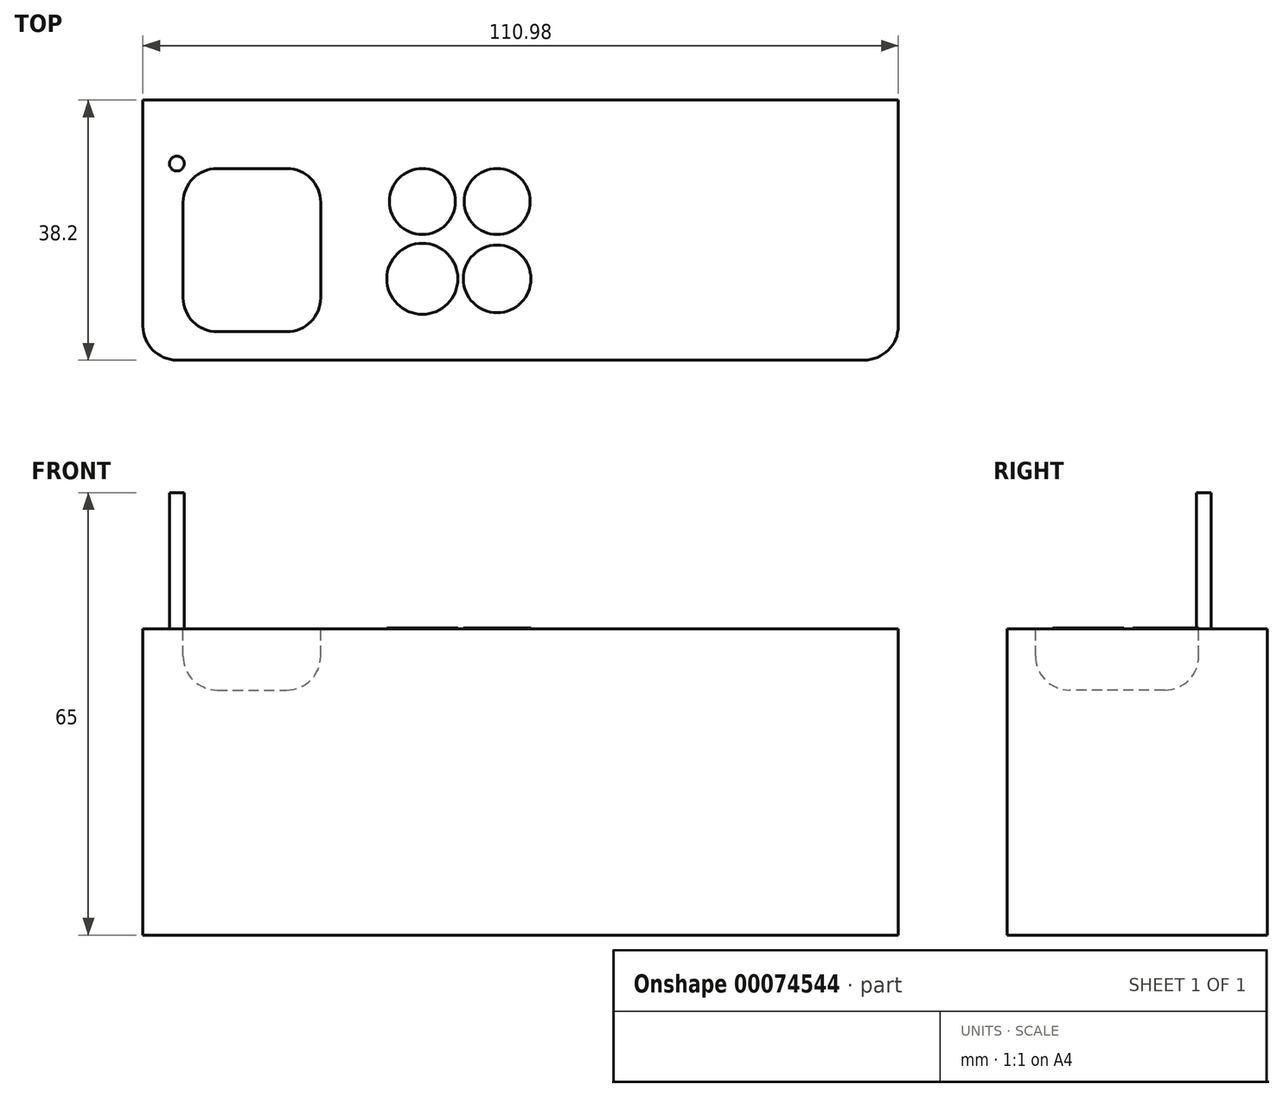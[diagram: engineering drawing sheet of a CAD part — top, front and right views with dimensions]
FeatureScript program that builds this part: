
annotation { "Feature Type Name" : "Feature", "Feature Type Description" : "" }
export const myFeature = defineFeature(function(context is Context, id is Id, definition is map)
    precondition{}
    {
        {
            var Q0;
            Q0=qCreatedBy(makeId("Top.planeOp"),FACE);
            var sketch = newSketch(context, id + "F0", { "sketchPlane" : qUnion([Q0])});
            skLineSegment(sketch, "E0.bottom", {"start": v(-50.94, 18.45) * mm, "end": v(60.04, 18.45) * mm});
            skLineSegment(sketch, "E0.top", {"start": v(-45.94, -19.75) * mm, "end": v(55.04, -19.75) * mm});
            skLineSegment(sketch, "E0.left", {"start": v(-50.94, 18.45) * mm, "end": v(-50.94, -14.75) * mm});
            skLineSegment(sketch, "E0.right", {"start": v(60.04, 18.45) * mm, "end": v(60.04, -14.75) * mm});
            skPoint(sketch, "E1.visualSharp", {"position": v(-50.94, -19.75) * mm});
            skArc(sketch, "E1.filletArc", {"start": v(-50.94, -14.75) * mm, "mid": v(-49.48, -18.29) * mm, "end": v(-45.94, -19.75) * mm});
            skPoint(sketch, "E2.visualSharp", {"position": v(60.04, -19.75) * mm});
            skArc(sketch, "E2.filletArc", {"start": v(55.04, -19.75) * mm, "mid": v(58.57, -18.29) * mm, "end": v(60.04, -14.75) * mm});
            skSolve(sketch);
        }
        {
            var Q0;
            Q0=makeQuery(id+"F0.imprint","IMPRINT",FACE,{"disambiguationData":[TD([[makeQuery(id+"F0.imprint","IMPRINT",EDGE,{"derivedFrom":sQuery(id+"F0.wireOp",EDGE,"E0.bottom")}),-1.0]])]});
            extrude(context, id + "F1", {"entities" : qUnion([Q0]), "depth" : 45 * mm});
        }
        {
            var Q0;
            Q0=makeQuery(id+"F1.opExtrude","CAP_FACE",FACE,{"disambiguationData":[OSD([sQuery(id+"F0.wireOp",EDGE,"E0.bottom"),sQuery(id+"F0.wireOp",EDGE,"E0.top"),sQuery(id+"F0.wireOp",EDGE,"E0.left"),sQuery(id+"F0.wireOp",EDGE,"E0.right")])],"isStart":false});
            var sketch = newSketch(context, id + "F2", { "sketchPlane" : qUnion([Q0])});
            skLineSegment(sketch, "E3", {"start": v(-20.23, 18.45) * mm, "end": v(-20.23, -19.75) * mm, "construction": true});
            skLineSegment(sketch, "E4", {"start": v(-20.23, -19.75) * mm, "end": v(11.04, -19.75) * mm, "construction": true});
            skLineSegment(sketch, "E5", {"start": v(11.04, -19.75) * mm, "end": v(11.04, 18.45) * mm, "construction": true});
            skLineSegment(sketch, "E6", {"start": v(11.04, 18.45) * mm, "end": v(-20.23, 18.45) * mm, "construction": true});
            skLineSegment(sketch, "E7.bottom", {"start": v(-40.03, 8.4) * mm, "end": v(-29.81, 8.4) * mm});
            skLineSegment(sketch, "E7.top", {"start": v(-40.03, -15.6) * mm, "end": v(-29.81, -15.6) * mm});
            skLineSegment(sketch, "E7.left", {"start": v(-45.03, 3.4) * mm, "end": v(-45.03, -10.6) * mm});
            skLineSegment(sketch, "E7.right", {"start": v(-24.81, 3.4) * mm, "end": v(-24.81, -10.6) * mm});
            skPoint(sketch, "E8.visualSharp", {"position": v(-45.03, 8.4) * mm});
            skArc(sketch, "E8.filletArc", {"start": v(-40.03, 8.4) * mm, "mid": v(-43.57, 6.94) * mm, "end": v(-45.03, 3.4) * mm});
            skPoint(sketch, "E9.visualSharp", {"position": v(-24.81, 8.4) * mm});
            skArc(sketch, "E9.filletArc", {"start": v(-24.81, 3.4) * mm, "mid": v(-26.28, 6.94) * mm, "end": v(-29.81, 8.4) * mm});
            skPoint(sketch, "E10.visualSharp", {"position": v(-45.03, -15.6) * mm});
            skArc(sketch, "E10.filletArc", {"start": v(-45.03, -10.6) * mm, "mid": v(-43.57, -14.13) * mm, "end": v(-40.03, -15.6) * mm});
            skPoint(sketch, "E11.visualSharp", {"position": v(-24.81, -15.6) * mm});
            skArc(sketch, "E11.filletArc", {"start": v(-29.81, -15.6) * mm, "mid": v(-26.28, -14.13) * mm, "end": v(-24.81, -10.6) * mm});
            skCircle(sketch, "E12", {"center": v(-45.95, 9.12) * mm, "radius": 1.1 * mm});
            skLineSegment(sketch, "E13.bottom", {"start": v(-15.37, 9.24) * mm, "end": v(6.58, 9.24) * mm, "construction": true});
            skLineSegment(sketch, "E13.top", {"start": v(-15.37, -13.5) * mm, "end": v(6.58, -13.5) * mm, "construction": true});
            skLineSegment(sketch, "E13.left", {"start": v(-15.37, 9.24) * mm, "end": v(-15.37, -13.5) * mm, "construction": true});
            skLineSegment(sketch, "E13.right", {"start": v(6.58, 9.24) * mm, "end": v(6.58, -13.5) * mm, "construction": true});
            skLineSegment(sketch, "E14", {"start": v(-15.37, -2.13) * mm, "end": v(-15.37, 9.24) * mm, "construction": true});
            skLineSegment(sketch, "E15", {"start": v(-15.37, -2.13) * mm, "end": v(-15.37, -13.5) * mm, "construction": true});
            skLineSegment(sketch, "E16", {"start": v(6.58, -2.13) * mm, "end": v(6.58, -13.5) * mm, "construction": true});
            skLineSegment(sketch, "E17", {"start": v(6.58, -2.13) * mm, "end": v(6.58, 9.24) * mm, "construction": true});
            skLineSegment(sketch, "E18", {"start": v(-4.4, 9.24) * mm, "end": v(-4.4, -13.5) * mm, "construction": true});
            skLineSegment(sketch, "E19", {"start": v(-15.37, -7.81) * mm, "end": v(6.58, -7.81) * mm, "construction": true});
            skLineSegment(sketch, "E20", {"start": v(-15.37, -2.13) * mm, "end": v(6.58, -2.13) * mm, "construction": true});
            skLineSegment(sketch, "E21", {"start": v(-15.37, 3.56) * mm, "end": v(6.58, 3.56) * mm, "construction": true});
            skLineSegment(sketch, "E22", {"start": v(-4.4, 3.56) * mm, "end": v(-15.37, 3.56) * mm, "construction": true});
            skLineSegment(sketch, "E23", {"start": v(-4.4, 3.56) * mm, "end": v(6.58, 3.56) * mm, "construction": true});
            skPoint(sketch, "E24", {"position": v(1.1, 3.56) * mm});
            skPoint(sketch, "E25", {"position": v(-9.88, 3.56) * mm});
            skPoint(sketch, "E26", {"position": v(-9.88, -7.81) * mm});
            skCircle(sketch, "E27", {"center": v(-9.88, 3.56) * mm, "radius": 4.85 * mm, "construction": true});
            skCircle(sketch, "E28", {"center": v(1.1, 3.56) * mm, "radius": 4.85 * mm, "construction": true});
            skCircle(sketch, "E29", {"center": v(-9.88, -7.81) * mm, "radius": 5.69 * mm, "construction": true});
            skLineSegment(sketch, "E30", {"start": v(-4.4, -7.81) * mm, "end": v(6.58, -7.81) * mm, "construction": true});
            skPoint(sketch, "E31", {"position": v(1.1, -7.81) * mm});
            skCircle(sketch, "E32", {"center": v(1.1, -7.81) * mm, "radius": 5.29 * mm, "construction": true});
            skCircle(sketch, "E33", {"center": v(1.1, 3.56) * mm, "radius": 4.85 * mm});
            skCircle(sketch, "E34", {"center": v(-9.88, 3.56) * mm, "radius": 4.85 * mm});
            skCircle(sketch, "E35", {"center": v(-9.88, -7.81) * mm, "radius": 5.22 * mm});
            skCircle(sketch, "E36", {"center": v(1.1, -7.81) * mm, "radius": 4.97 * mm});
            skSolve(sketch);
        }
        {
            var Q0;
            Q0=makeQuery(id+"F2.imprint","IMPRINT",FACE,{"disambiguationData":[TD([[makeQuery(id+"F2.imprint","IMPRINT",EDGE,{"derivedFrom":sQuery(id+"F2.wireOp",EDGE,"E33")}),1.0]])]});
            var Q1;
            Q1=makeQuery(id+"F2.imprint","IMPRINT",FACE,{"disambiguationData":[TD([[makeQuery(id+"F2.imprint","IMPRINT",EDGE,{"derivedFrom":sQuery(id+"F2.wireOp",EDGE,"E34")}),1.0]])]});
            var Q2;
            Q2=makeQuery(id+"F2.imprint","IMPRINT",FACE,{"disambiguationData":[TD([[makeQuery(id+"F2.imprint","IMPRINT",EDGE,{"derivedFrom":sQuery(id+"F2.wireOp",EDGE,"E35")}),1.0]])]});
            var Q3;
            Q3=makeQuery(id+"F2.imprint","IMPRINT",FACE,{"disambiguationData":[TD([[makeQuery(id+"F2.imprint","IMPRINT",EDGE,{"derivedFrom":sQuery(id+"F2.wireOp",EDGE,"E36")}),1.0]])]});
            extrude(context, id + "F3", {"entities" : qUnion([Q0, Q1, Q2, Q3]), "operationType" : NewBodyOperationType.ADD, "depth" : 0.1 * mm});
        }
        {
            var Q0;
            Q0=makeQuery(id+"F2.imprint","IMPRINT",FACE,{"disambiguationData":[TD([[makeQuery(id+"F2.imprint","IMPRINT",EDGE,{"derivedFrom":sQuery(id+"F2.wireOp",EDGE,"E7.bottom")}),-1.0]])]});
            extrude(context, id + "F4", {"entities" : qUnion([Q0]), "operationType" : NewBodyOperationType.REMOVE, "oppositeDirection" : true, "depth" : 9 * mm});
        }
        {
            var Q0;
            Q0=makeQuery(id+"F4.boolean.opBoolean","COPY",EDGE,{"derivedFrom":makeQuery(id+"F4.opExtrude","CAP_EDGE",EDGE,{"disambiguationData":[OSD([sQuery(id+"F2.wireOp",EDGE,"E8.filletArc")])],"isStart":false})});
            var Q1;
            Q1=makeQuery(id+"F4.boolean.opBoolean","COPY",EDGE,{"derivedFrom":makeQuery(id+"F4.opExtrude","CAP_EDGE",EDGE,{"disambiguationData":[OSD([sQuery(id+"F2.wireOp",EDGE,"E7.bottom")])],"isStart":false})});
            fillet(context, id + "F5", {"entities" : qUnion([Q0, Q1]), "radius" : 5 * mm, "tangentPropagation" : true, "allowEdgeOverflow" : false});
        }
        {
            var Q0;
            Q0=makeQuery(id+"F2.imprint","IMPRINT",FACE,{"disambiguationData":[TD([[makeQuery(id+"F2.imprint","IMPRINT",EDGE,{"derivedFrom":sQuery(id+"F2.wireOp",EDGE,"E12")}),1.0]])]});
            extrude(context, id + "F6", {"entities" : qUnion([Q0]), "operationType" : NewBodyOperationType.ADD, "depth" : 20 * mm});
        }
    });
